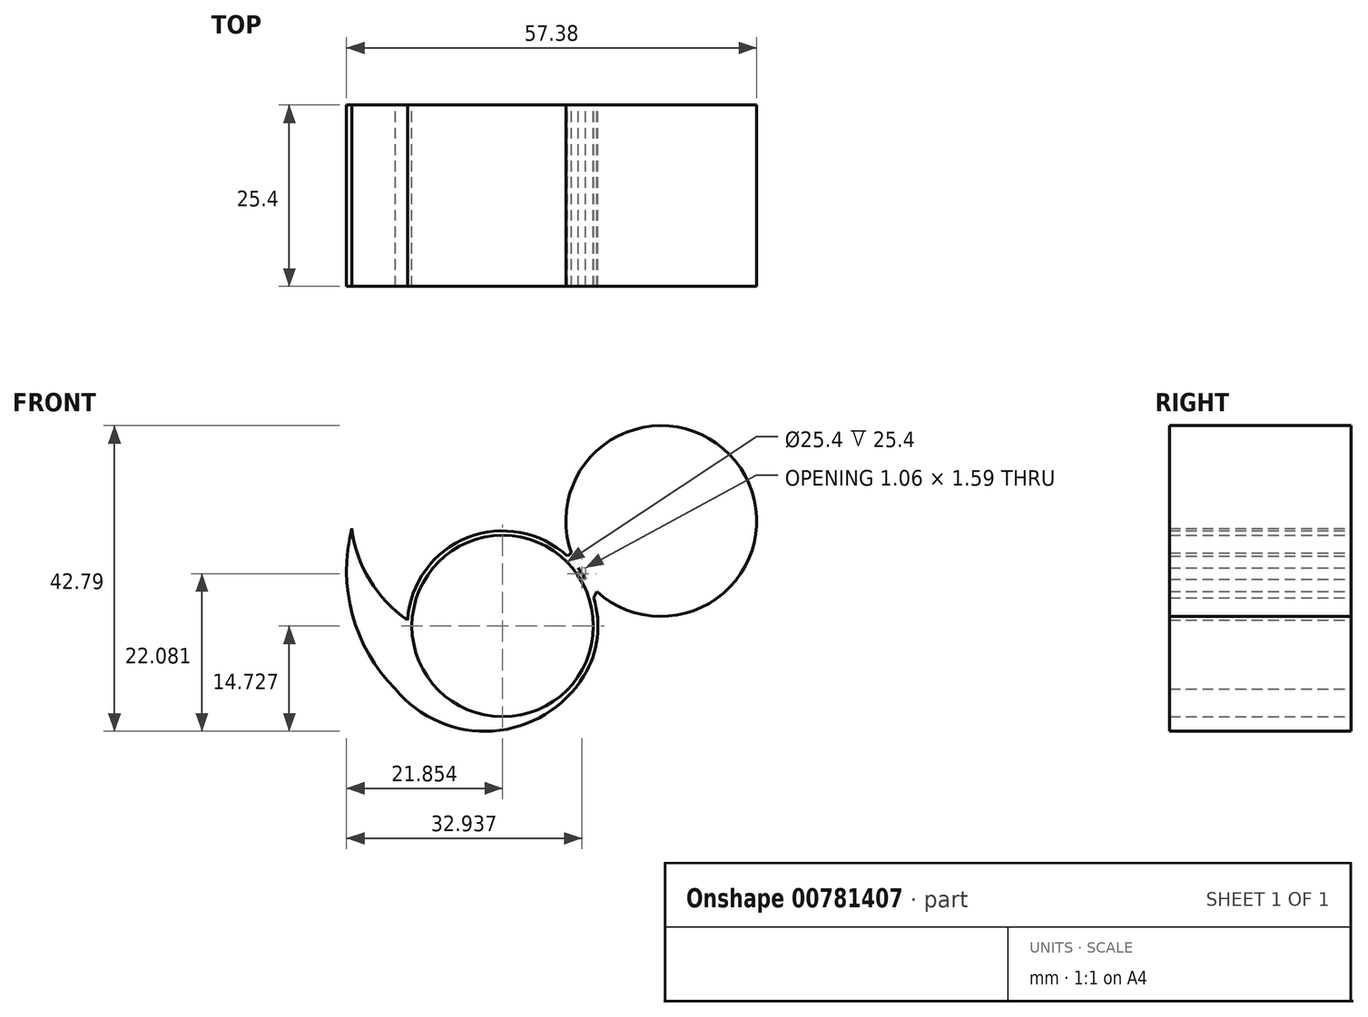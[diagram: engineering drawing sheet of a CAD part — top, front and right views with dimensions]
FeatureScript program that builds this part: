
annotation { "Feature Type Name" : "Feature", "Feature Type Description" : "" }
export const myFeature = defineFeature(function(context is Context, id is Id, definition is map)
    precondition{}
    {
        {
            var Q0;
            Q0=qCreatedBy(makeId("Front.planeOp"),FACE);
            var sketch = newSketch(context, id + "F0", { "sketchPlane" : qUnion([Q0])});
            skCircle(sketch, "E0", {"center": v(0, 0) * mm, "radius": 13.34 * mm});
            skArc(sketch, "E1", {"start": v(-10.82, -21.7) * mm, "mid": v(-18.13, -2) * mm, "end": v(-35.48, -13.84) * mm});
            skArc(sketch, "E2", {"start": v(-37.2, -23.54) * mm, "mid": v(-23.54, -29.4) * mm, "end": v(-10.82, -21.7) * mm});
            skLineSegment(sketch, "E3", {"start": v(-9.45, -10.73) * mm, "end": v(-8.98, -9.86) * mm});
            skLineSegment(sketch, "E4", {"start": v(-13.1, -4.93) * mm, "end": v(-12.56, -4.49) * mm});
            skCircle(sketch, "E5", {"center": v(0, 0) * mm, "radius": 13.35 * mm});
            skArc(sketch, "E6", {"start": v(-43.29, -1.07) * mm, "mid": v(-43.2, -13.1) * mm, "end": v(-37.2, -23.54) * mm});
            skArc(sketch, "E7", {"start": v(-43.29, -1.07) * mm, "mid": v(-40.77, -8.3) * mm, "end": v(-35.48, -13.84) * mm});
            skCircle(sketch, "E8", {"center": v(-22.18, -14.71) * mm, "radius": 12.7 * mm});
            skSolve(sketch);
        }
        {
            var Q0;
            {var subQ0=sQuery(id+"F0.wireOp",EDGE,"E3");var subQ1=sQuery(id+"F0.wireOp",EDGE,"E1");var subQ2=makeQuery(id+"F0.imprint","INTERSECT",VERTEX,{"derivedFrom":[subQ1,subQ0]});Q0=makeQuery(id+"F0.imprint","IMPRINT",FACE,{"disambiguationData":[TD([[makeQuery(id+"F0.imprint","IMPRINT",EDGE,{"disambiguationData":[TD([[subQ2,-1.0]])],"derivedFrom":subQ1}),-1.0]])]});}
            var Q1;
            {var subQ0=sQuery(id+"F0.wireOp",EDGE,"E4");var subQ1=sQuery(id+"F0.wireOp",EDGE,"E1");var subQ2=makeQuery(id+"F0.imprint","INTERSECT",VERTEX,{"derivedFrom":[subQ1,subQ0]});Q1=makeQuery(id+"F0.imprint","IMPRINT",FACE,{"disambiguationData":[TD([[makeQuery(id+"F0.imprint","IMPRINT",EDGE,{"disambiguationData":[TD([[subQ2,1.0]])],"derivedFrom":subQ1}),-1.0]])]});}
            var Q2;
            {var subQ0=sQuery(id+"F0.wireOp",EDGE,"E3");var subQ1=sQuery(id+"F0.wireOp",EDGE,"E0");var subQ2=makeQuery(id+"F0.imprint","INTERSECT",VERTEX,{"derivedFrom":[subQ1,subQ0]});Q2=makeQuery(id+"F0.imprint","IMPRINT",FACE,{"disambiguationData":[TD([[makeQuery(id+"F0.imprint","IMPRINT",EDGE,{"disambiguationData":[TD([[subQ2,-1.0]])],"derivedFrom":subQ1}),-1.0]])]});}
            var Q3;
            {var subQ0=sQuery(id+"F0.wireOp",EDGE,"E4");var subQ1=sQuery(id+"F0.wireOp",EDGE,"E0");var subQ2=makeQuery(id+"F0.imprint","INTERSECT",VERTEX,{"derivedFrom":[subQ1,subQ0]});Q3=makeQuery(id+"F0.imprint","IMPRINT",FACE,{"disambiguationData":[TD([[makeQuery(id+"F0.imprint","IMPRINT",EDGE,{"disambiguationData":[TD([[subQ2,-1.0]])],"derivedFrom":subQ1}),-1.0]])]});}
            var Q4;
            {var subQ0=sQuery(id+"F0.wireOp",EDGE,"E3");var subQ1=sQuery(id+"F0.wireOp",EDGE,"E0");var subQ2=makeQuery(id+"F0.imprint","INTERSECT",VERTEX,{"derivedFrom":[subQ1,subQ0]});Q4=makeQuery(id+"F0.imprint","IMPRINT",FACE,{"disambiguationData":[TD([[makeQuery(id+"F0.imprint","IMPRINT",EDGE,{"disambiguationData":[TD([[subQ2,1.0]])],"derivedFrom":subQ1}),-1.0]])]});}
            var Q5;
            {var subQ7=sQuery(id+"F0.wireOp",EDGE,"E2");Q5=makeQuery(id+"F0.imprint","IMPRINT",FACE,{"disambiguationData":[TD([[makeQuery(id+"F0.imprint","IMPRINT",EDGE,{"derivedFrom":subQ7}),1.0]])]});}
            var Q6;
            {var subQ0=sQuery(id+"F0.wireOp",EDGE,"E0");var subQ1=makeQuery(id+"F0.imprint","INTERSECT",VERTEX,{"derivedFrom":[subQ0,sQuery(id+"F0.wireOp",EDGE,"E4")]});Q6=makeQuery(id+"F0.imprint","IMPRINT",FACE,{"disambiguationData":[TD([[makeQuery(id+"F0.imprint","IMPRINT",EDGE,{"disambiguationData":[TD([[subQ1,-1.0]])],"derivedFrom":subQ0}),1.0]])]});}
            extrude(context, id + "F1", {"entities" : qUnion([Q0, Q1, Q2, Q3, Q4, Q5, Q6]), "depth" : 25.4 * mm, "offsetDistance" : 25.4 * mm});
        }
    });
